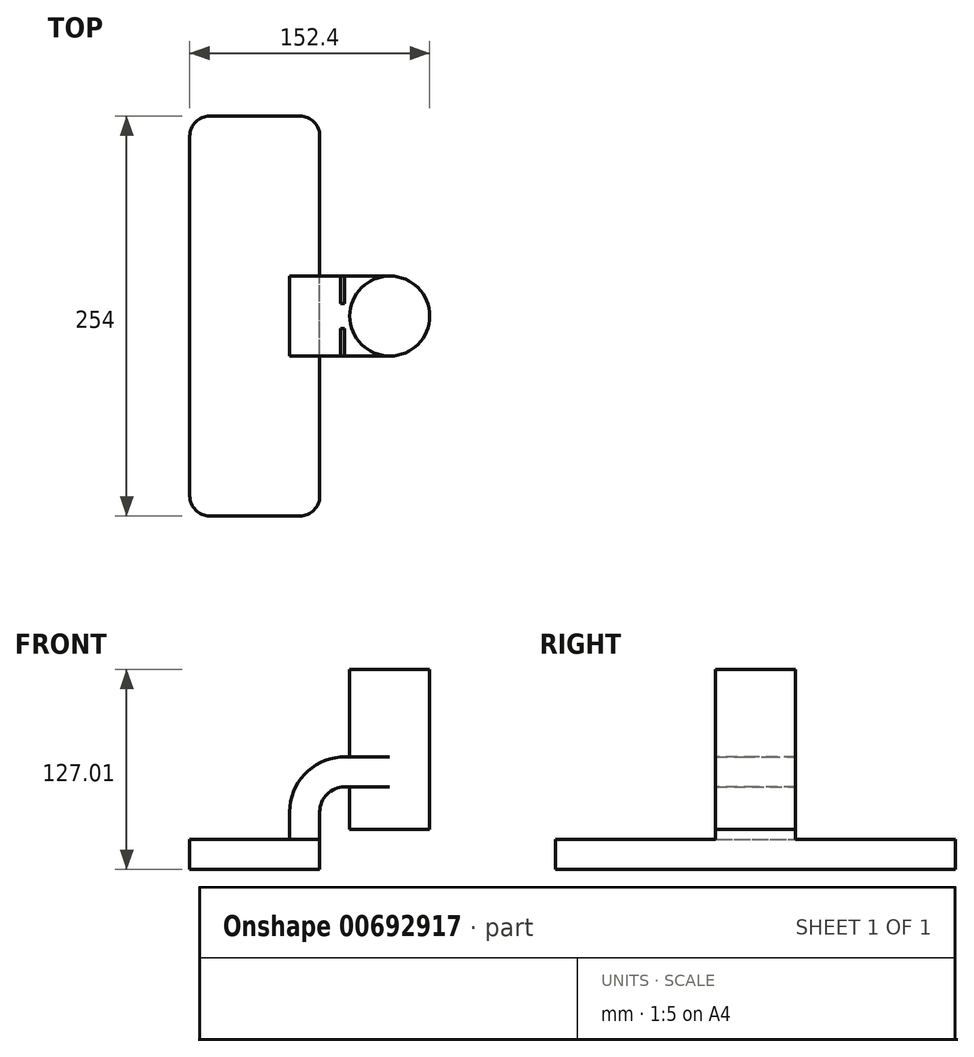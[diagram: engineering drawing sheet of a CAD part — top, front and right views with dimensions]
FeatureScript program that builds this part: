
annotation { "Feature Type Name" : "Feature", "Feature Type Description" : "" }
export const myFeature = defineFeature(function(context is Context, id is Id, definition is map)
    precondition{}
    {
        {
            var Q0;
            Q0=qCreatedBy(makeId("Front.planeOp"),FACE);
            var sketch = newSketch(context, id + "F0", { "sketchPlane" : qUnion([Q0])});
            skLineSegment(sketch, "E0.bottom", {"start": v(-39.77, 9.52) * mm, "end": v(42.78, 9.53) * mm});
            skLineSegment(sketch, "E0.top", {"start": v(-39.77, -9.53) * mm, "end": v(42.78, -9.52) * mm});
            skLineSegment(sketch, "E0.left", {"start": v(-39.77, 9.53) * mm, "end": v(-39.77, -9.53) * mm});
            skLineSegment(sketch, "E0.right", {"start": v(42.78, 9.53) * mm, "end": v(42.78, -9.53) * mm});
            skPoint(sketch, "E0.middle", {"position": v(1.5, 0) * mm});
            skLineSegment(sketch, "E1.bottom", {"start": v(61.83, 15.88) * mm, "end": v(112.63, 15.88) * mm});
            skLineSegment(sketch, "E1.top", {"start": v(61.83, 117.47) * mm, "end": v(112.63, 117.47) * mm});
            skLineSegment(sketch, "E1.left", {"start": v(61.83, 15.87) * mm, "end": v(61.83, 117.47) * mm});
            skLineSegment(sketch, "E1.right", {"start": v(112.63, 15.87) * mm, "end": v(112.63, 117.47) * mm});
            skPoint(sketch, "E1.middle", {"position": v(87.23, 66.67) * mm});
            skLineSegment(sketch, "E2", {"start": v(42.78, 9.53) * mm, "end": v(42.78, 27) * mm});
            skArc(sketch, "E3", {"start": v(42.78, 27) * mm, "mid": v(47.43, 38.23) * mm, "end": v(58.65, 42.88) * mm});
            skLineSegment(sketch, "E4", {"start": v(58.65, 42.88) * mm, "end": v(87.23, 42.88) * mm});
            skPoint(sketch, "E4.endSnap0", {"position": v(87.23, 15.87) * mm});
            skLineSegment(sketch, "E5.0", {"start": v(58.65, 61.93) * mm, "end": v(87.43, 61.93) * mm});
            skArc(sketch, "E5.1", {"start": v(23.73, 27) * mm, "mid": v(33.96, 51.7) * mm, "end": v(58.65, 61.93) * mm});
            skLineSegment(sketch, "E5.2", {"start": v(23.73, 9.53) * mm, "end": v(23.73, 27) * mm});
            skLineSegment(sketch, "E6", {"start": v(87.23, 15.87) * mm, "end": v(87.23, 117.47) * mm});
            skFitSpline(sketch, "E7", {"points": [v(-39.77, 9.52) * mm, v(58.65, 61.93) * mm], "startDerivative": vector(7.8, 55.83) * mm, "endDerivative": vector(193.63, 6.22) * mm});
            skSolve(sketch);
        }
        {
            var Q0;
            Q0=makeQuery(id+"F0.imprint","IMPRINT",FACE,{"disambiguationData":[TD([[makeQuery(id+"F0.imprint","IMPRINT",EDGE,{"derivedFrom":sQuery(id+"F0.wireOp",EDGE,"E0.top")}),1.0]])]});
            extrude(context, id + "F1", {"entities" : qUnion([Q0]), "endBound" : BoundingType.SYMMETRIC, "depth" : 254 * mm, "offsetDistance" : 25.4 * mm});
        }
        {
            var Q0;
            {var subQ0=sQuery(id+"F0.wireOp",EDGE,"E4");var subQ1=sQuery(id+"F0.wireOp",EDGE,"E1.left");var subQ2=makeQuery(id+"F0.imprint","INTERSECT",VERTEX,{"derivedFrom":[subQ1,subQ0]});Q0=makeQuery(id+"F0.imprint","IMPRINT",FACE,{"disambiguationData":[TD([[makeQuery(id+"F0.imprint","IMPRINT",EDGE,{"disambiguationData":[TD([[subQ2,-1.0]])],"derivedFrom":subQ1}),-1.0]])]});}
            var Q1;
            {var subQ1=sQuery(id+"F0.wireOp",EDGE,"E2");Q1=makeQuery(id+"F0.imprint","IMPRINT",FACE,{"disambiguationData":[TD([[makeQuery(id+"F0.imprint","IMPRINT",EDGE,{"derivedFrom":subQ1}),1.0]])]});}
            extrude(context, id + "F2", {"entities" : qUnion([Q0, Q1]), "operationType" : NewBodyOperationType.ADD, "endBound" : BoundingType.SYMMETRIC, "depth" : 50.8 * mm, "offsetDistance" : 25.4 * mm});
        }
        {
            var Q0;
            Q0=makeQuery(id+"F0.imprint","IMPRINT",FACE,{"disambiguationData":[TD([[makeQuery(id+"F0.imprint","IMPRINT",EDGE,{"derivedFrom":sQuery(id+"F0.wireOp",EDGE,"E5.1")}),1.0]])]});
            extrude(context, id + "F3", {"entities" : qUnion([Q0]), "operationType" : NewBodyOperationType.ADD, "endBound" : BoundingType.SYMMETRIC, "depth" : 15.88 * mm, "offsetDistance" : 25.4 * mm});
        }
        {
            var Q0;
            {var subQ0=sQuery(id+"F0.wireOp",EDGE,"E1.right");Q0=makeQuery(id+"F0.imprint","IMPRINT",FACE,{"disambiguationData":[TD([[makeQuery(id+"F0.imprint","IMPRINT",EDGE,{"derivedFrom":subQ0}),1.0]])]});}
            var Q1;
            Q1=sQuery(id+"F0.wireOp",EDGE,"E6");
            revolve(context, id + "F4", {"operationType" : NewBodyOperationType.ADD, "entities" : qUnion([Q0]), "axis" : qUnion([Q1]), "revolveType" : RevolveType.FULL});
        }
        {
            var Q0;
            Q0=makeQuery(id+"F1.opExtrude","CAP_EDGE",EDGE,{"disambiguationData":[OSD([sQuery(id+"F0.wireOp",EDGE,"E0.left")])],"isStart":false});
            var Q1;
            Q1=makeQuery(id+"F1.opExtrude","CAP_EDGE",EDGE,{"disambiguationData":[OSD([sQuery(id+"F0.wireOp",EDGE,"E0.right")])],"isStart":false});
            var Q2;
            Q2=makeQuery(id+"F1.opExtrude","CAP_EDGE",EDGE,{"disambiguationData":[OSD([sQuery(id+"F0.wireOp",EDGE,"E0.right")])],"isStart":true});
            var Q3;
            Q3=makeQuery(id+"F1.opExtrude","CAP_EDGE",EDGE,{"disambiguationData":[OSD([sQuery(id+"F0.wireOp",EDGE,"E0.left")])],"isStart":true});
            fillet(context, id + "F5", {"entities" : qUnion([Q0, Q1, Q2, Q3]), "radius" : 12.7 * mm, "tangentPropagation" : true, "allowEdgeOverflow" : false});
        }
    });
